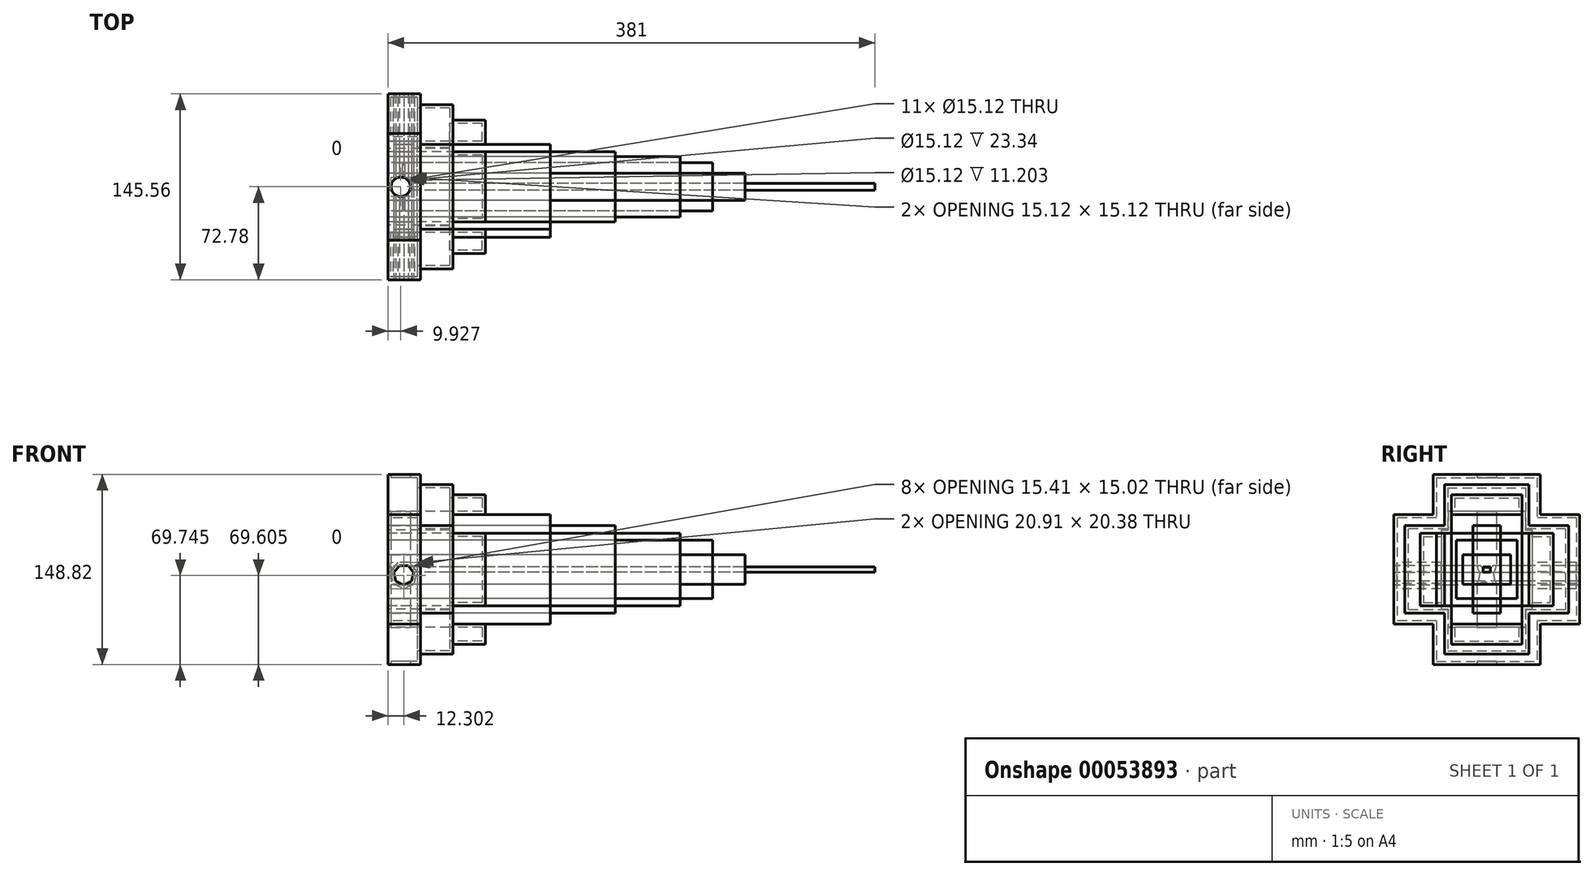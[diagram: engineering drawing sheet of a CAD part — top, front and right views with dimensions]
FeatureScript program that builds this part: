
annotation { "Feature Type Name" : "Feature", "Feature Type Description" : "" }
export const myFeature = defineFeature(function(context is Context, id is Id, definition is map)
    precondition{}
    {
        {
            var Q0;
            Q0=qCreatedBy(makeId("Top.planeOp"),FACE);
            var sketch = newSketch(context, id + "F0", { "sketchPlane" : qUnion([Q0])});
            skCircle(sketch, "E0", {"center": v(-6.98, 31.64) * mm, "radius": 25.79 * mm});
            skPoint(sketch, "E0.first.point", {"position": v(-32.77, 31.84) * mm});
            skPoint(sketch, "E0.second.point", {"position": v(18.77, 33.14) * mm});
            skPoint(sketch, "E0.third.point", {"position": v(-22.31, 52.38) * mm});
            skCircle(sketch, "E1", {"center": v(6.7, 18.5) * mm, "radius": 18.97 * mm});
            skPoint(sketch, "E1.second.point", {"position": v(2.52, 0) * mm});
            skCircle(sketch, "E2", {"center": v(-19.83, 38.18) * mm, "radius": 14.41 * mm});
            skCircle(sketch, "E3", {"center": v(-6.25, 28.75) * mm, "radius": 16.52 * mm});
            skPoint(sketch, "E3.third.point", {"position": v(-16.71, 41.55) * mm});
            skCircle(sketch, "E4", {"center": v(-7.59, 13.75) * mm, "radius": 15.06 * mm});
            skPoint(sketch, "E4.third.point", {"position": v(-8.92, 28.75) * mm});
            skCircle(sketch, "E5", {"center": v(-26.31, 19.65) * mm, "radius": 19.63 * mm});
            skCircle(sketch, "E6", {"center": v(3, 45.23) * mm, "radius": 20.34 * mm});
            skPoint(sketch, "E6.second.point", {"position": v(14.1, 62.27) * mm});
            skPoint(sketch, "E6.third.point", {"position": v(21.94, 37.81) * mm});
            skCircle(sketch, "E7", {"center": v(-21.54, 45.6) * mm, "radius": 21.06 * mm});
            skPoint(sketch, "E7.second.point", {"position": v(-35.94, 60.96) * mm});
            skPoint(sketch, "E7.third.point", {"position": v(-42.1, 50.13) * mm});
            skCircle(sketch, "E8", {"center": v(3.75, 38.24) * mm, "radius": 15.83 * mm});
            skPoint(sketch, "E8.second.point", {"position": v(18.2, 44.72) * mm});
            skPoint(sketch, "E8.third.point", {"position": v(6.7, 22.69) * mm});
            skCircle(sketch, "E9", {"center": v(-6.92, 15.23) * mm, "radius": 13.67 * mm});
            skPoint(sketch, "E9.first.point", {"position": v(-10.18, 1.96) * mm});
            skPoint(sketch, "E9.third.point", {"position": v(4.54, 22.69) * mm});
            skCircle(sketch, "E10", {"center": v(21.82, 32.35) * mm, "radius": 30.95 * mm});
            skPoint(sketch, "E10.second.point", {"position": v(52.56, 28.75) * mm});
            skPoint(sketch, "E10.third.point", {"position": v(26.6, 1.77) * mm});
            skCircle(sketch, "E11", {"center": v(-43.67, 28.86) * mm, "radius": 33.35 * mm});
            skPoint(sketch, "E11.first.point", {"position": v(-77.02, 28.66) * mm});
            skPoint(sketch, "E11.second.point", {"position": v(-10.4, 31.14) * mm});
            skPoint(sketch, "E11.third.point", {"position": v(-75.16, 39.86) * mm});
            skCircle(sketch, "E12", {"center": v(-4.85, 1.88) * mm, "radius": 27.18 * mm});
            skPoint(sketch, "E12.second.point", {"position": v(-5.13, -25.3) * mm});
            skPoint(sketch, "E12.third.point", {"position": v(-4.57, -25.3) * mm});
            skCircle(sketch, "E13", {"center": v(-7.9, 52.7) * mm, "radius": 23.97 * mm});
            skPoint(sketch, "E13.second.point", {"position": v(-8.92, 76.65) * mm});
            skPoint(sketch, "E13.third.point", {"position": v(-28.09, 65.62) * mm});
            skSolve(sketch);
        }
        {
            var Q0;
            Q0=qCreatedBy(makeId("Right.planeOp"),FACE);
            var sketch = newSketch(context, id + "F1", { "sketchPlane" : qUnion([Q0])});
            skLineSegment(sketch, "E14.rect.bottom", {"start": v(-23.76, 22.87) * mm, "end": v(23.76, 22.87) * mm});
            skLineSegment(sketch, "E14.rect.top", {"start": v(-23.76, -22.87) * mm, "end": v(23.76, -22.87) * mm});
            skLineSegment(sketch, "E14.rect.left", {"start": v(-23.76, 22.87) * mm, "end": v(-23.76, -22.87) * mm});
            skLineSegment(sketch, "E14.rect.right", {"start": v(23.76, 22.87) * mm, "end": v(23.76, -22.87) * mm});
            skPoint(sketch, "E14.rect.middle", {"position": v(0, 0) * mm});
            skLineSegment(sketch, "E15.rect.bottom", {"start": v(-10.69, 45.28) * mm, "end": v(10.69, 45.28) * mm});
            skLineSegment(sketch, "E15.rect.top", {"start": v(-10.69, -45.28) * mm, "end": v(10.69, -45.28) * mm});
            skLineSegment(sketch, "E15.rect.left", {"start": v(-10.69, 45.28) * mm, "end": v(-10.69, -45.28) * mm});
            skLineSegment(sketch, "E15.rect.right", {"start": v(10.69, 45.28) * mm, "end": v(10.69, -45.28) * mm});
            skLineSegment(sketch, "E16.rect.bottom", {"start": v(64.19, 34.26) * mm, "end": v(-64.19, 34.26) * mm});
            skLineSegment(sketch, "E16.rect.top", {"start": v(64.19, -34.26) * mm, "end": v(-64.19, -34.26) * mm});
            skLineSegment(sketch, "E16.rect.left", {"start": v(64.19, 34.26) * mm, "end": v(64.19, -34.26) * mm});
            skLineSegment(sketch, "E16.rect.right", {"start": v(-64.19, 34.26) * mm, "end": v(-64.19, -34.26) * mm});
            skLineSegment(sketch, "E17.rect.bottom", {"start": v(-33.1, 66.38) * mm, "end": v(33.1, 66.38) * mm});
            skLineSegment(sketch, "E17.rect.top", {"start": v(-33.1, -66.38) * mm, "end": v(33.1, -66.38) * mm});
            skLineSegment(sketch, "E17.rect.left", {"start": v(-33.1, 66.38) * mm, "end": v(-33.1, -66.38) * mm});
            skLineSegment(sketch, "E17.rect.right", {"start": v(33.1, 66.38) * mm, "end": v(33.1, -66.38) * mm});
            skLineSegment(sketch, "E18.rect.bottom", {"start": v(5.37, 6.07) * mm, "end": v(-5.37, 6.07) * mm});
            skLineSegment(sketch, "E18.rect.top", {"start": v(5.37, -6.07) * mm, "end": v(-5.37, -6.07) * mm});
            skLineSegment(sketch, "E18.rect.left", {"start": v(5.37, 6.07) * mm, "end": v(5.37, -6.07) * mm});
            skLineSegment(sketch, "E18.rect.right", {"start": v(-5.37, 6.07) * mm, "end": v(-5.37, -6.07) * mm});
            skLineSegment(sketch, "E19.rect.bottom", {"start": v(2.76, 2.15) * mm, "end": v(-2.76, 2.15) * mm});
            skLineSegment(sketch, "E19.rect.top", {"start": v(2.76, -2.15) * mm, "end": v(-2.76, -2.15) * mm});
            skLineSegment(sketch, "E19.rect.left", {"start": v(2.76, 2.15) * mm, "end": v(2.76, -2.15) * mm});
            skLineSegment(sketch, "E19.rect.right", {"start": v(-2.76, 2.15) * mm, "end": v(-2.76, -2.15) * mm});
            skLineSegment(sketch, "E20.rect.bottom", {"start": v(18.81, 11.67) * mm, "end": v(-18.81, 11.67) * mm});
            skLineSegment(sketch, "E20.rect.top", {"start": v(18.81, -11.67) * mm, "end": v(-18.81, -11.67) * mm});
            skLineSegment(sketch, "E20.rect.left", {"start": v(18.81, 11.67) * mm, "end": v(18.81, -11.67) * mm});
            skLineSegment(sketch, "E20.rect.right", {"start": v(-18.81, 11.67) * mm, "end": v(-18.81, -11.67) * mm});
            skLineSegment(sketch, "E21.rect.bottom", {"start": v(-52.14, 28.47) * mm, "end": v(52.14, 28.47) * mm});
            skLineSegment(sketch, "E21.rect.top", {"start": v(-52.14, -28.47) * mm, "end": v(52.14, -28.47) * mm});
            skLineSegment(sketch, "E21.rect.left", {"start": v(-52.14, 28.47) * mm, "end": v(-52.14, -28.47) * mm});
            skLineSegment(sketch, "E21.rect.right", {"start": v(52.14, 28.47) * mm, "end": v(52.14, -28.47) * mm});
            skLineSegment(sketch, "E22.rect.bottom", {"start": v(-27.5, 58.54) * mm, "end": v(27.5, 58.54) * mm});
            skLineSegment(sketch, "E22.rect.top", {"start": v(-27.5, -58.54) * mm, "end": v(27.5, -58.54) * mm});
            skLineSegment(sketch, "E22.rect.left", {"start": v(-27.5, 58.54) * mm, "end": v(-27.5, -58.54) * mm});
            skLineSegment(sketch, "E22.rect.right", {"start": v(27.5, 58.54) * mm, "end": v(27.5, -58.54) * mm});
            skLineSegment(sketch, "E23.rect.bottom", {"start": v(72.78, 42.85) * mm, "end": v(-72.78, 42.85) * mm});
            skLineSegment(sketch, "E23.rect.top", {"start": v(72.78, -42.85) * mm, "end": v(-72.78, -42.85) * mm});
            skLineSegment(sketch, "E23.rect.left", {"start": v(72.78, 42.85) * mm, "end": v(72.78, -42.85) * mm});
            skLineSegment(sketch, "E23.rect.right", {"start": v(-72.78, 42.85) * mm, "end": v(-72.78, -42.85) * mm});
            skLineSegment(sketch, "E24.rect.bottom", {"start": v(-41.87, 74.4) * mm, "end": v(41.87, 74.4) * mm});
            skLineSegment(sketch, "E24.rect.top", {"start": v(-41.87, -74.4) * mm, "end": v(41.87, -74.4) * mm});
            skLineSegment(sketch, "E24.rect.left", {"start": v(-41.87, 74.4) * mm, "end": v(-41.87, -74.4) * mm});
            skLineSegment(sketch, "E24.rect.right", {"start": v(41.87, 74.4) * mm, "end": v(41.87, -74.4) * mm});
            skSolve(sketch);
        }
        {
            var Q0;
            Q0 = qSketchRegion(id + "F1", true);
            extrude(context, id + "F2", {"entities" : qUnion([Q0]), "depth" : 25.4 * mm});
        }
        {
            var Q0;
            {var subQ0=sQuery(id+"F1.wireOp",EDGE,"E16.rect.right");Q0=makeQuery(id+"F1.imprint","IMPRINT",FACE,{"disambiguationData":[TD([[makeQuery(id+"F1.imprint","IMPRINT",EDGE,{"derivedFrom":subQ0}),1.0]])]});}
            var Q1;
            {var subQ8=sQuery(id+"F1.wireOp",EDGE,"E16.rect.left");Q1=makeQuery(id+"F1.imprint","IMPRINT",FACE,{"disambiguationData":[TD([[makeQuery(id+"F1.imprint","IMPRINT",EDGE,{"derivedFrom":subQ8}),-1.0]])]});}
            var Q2;
            {var subQ2=sQuery(id+"F1.wireOp",EDGE,"E17.rect.bottom");Q2=makeQuery(id+"F1.imprint","IMPRINT",FACE,{"disambiguationData":[TD([[makeQuery(id+"F1.imprint","IMPRINT",EDGE,{"derivedFrom":subQ2}),-1.0]])]});}
            var Q3;
            {var subQ2=sQuery(id+"F1.wireOp",EDGE,"E17.rect.top");Q3=makeQuery(id+"F1.imprint","IMPRINT",FACE,{"disambiguationData":[TD([[makeQuery(id+"F1.imprint","IMPRINT",EDGE,{"derivedFrom":subQ2}),1.0]])]});}
            extrude(context, id + "F3", {"entities" : qUnion([Q0, Q1, Q2, Q3]), "operationType" : NewBodyOperationType.ADD, "depth" : 50.8 * mm});
        }
        {
            var Q0;
            {var subQ0=sQuery(id+"F1.wireOp",EDGE,"E17.rect.right");var subQ1=sQuery(id+"F1.wireOp",EDGE,"E16.rect.bottom");var subQ2=makeQuery(id+"F1.imprint","INTERSECT",VERTEX,{"derivedFrom":[subQ1,subQ0]});Q0=makeQuery(id+"F1.imprint","IMPRINT",FACE,{"disambiguationData":[TD([[makeQuery(id+"F1.imprint","IMPRINT",EDGE,{"disambiguationData":[TD([[subQ2,-1.0]])],"derivedFrom":subQ1}),-1.0]])]});}
            var Q1;
            {var subQ0=sQuery(id+"F1.wireOp",EDGE,"E24.rect.right");var subQ1=sQuery(id+"F1.wireOp",EDGE,"E16.rect.bottom");var subQ2=makeQuery(id+"F1.imprint","INTERSECT",VERTEX,{"derivedFrom":[subQ1,subQ0]});Q1=makeQuery(id+"F1.imprint","IMPRINT",FACE,{"disambiguationData":[TD([[makeQuery(id+"F1.imprint","IMPRINT",EDGE,{"disambiguationData":[TD([[subQ2,-1.0]])],"derivedFrom":subQ1}),1.0]])]});}
            var Q2;
            {var subQ0=sQuery(id+"F1.wireOp",EDGE,"E17.rect.right");var subQ1=sQuery(id+"F1.wireOp",EDGE,"E16.rect.bottom");var subQ2=makeQuery(id+"F1.imprint","INTERSECT",VERTEX,{"derivedFrom":[subQ1,subQ0]});Q2=makeQuery(id+"F1.imprint","IMPRINT",FACE,{"disambiguationData":[TD([[makeQuery(id+"F1.imprint","IMPRINT",EDGE,{"disambiguationData":[TD([[subQ2,-1.0]])],"derivedFrom":subQ1}),1.0]])]});}
            var Q3;
            {var subQ0=sQuery(id+"F1.wireOp",EDGE,"E22.rect.left");var subQ1=sQuery(id+"F1.wireOp",EDGE,"E16.rect.bottom");var subQ2=makeQuery(id+"F1.imprint","INTERSECT",VERTEX,{"derivedFrom":[subQ1,subQ0]});Q3=makeQuery(id+"F1.imprint","IMPRINT",FACE,{"disambiguationData":[TD([[makeQuery(id+"F1.imprint","IMPRINT",EDGE,{"disambiguationData":[TD([[subQ2,-1.0]])],"derivedFrom":subQ1}),-1.0]])]});}
            var Q4;
            {var subQ0=sQuery(id+"F1.wireOp",EDGE,"E22.rect.left");var subQ1=sQuery(id+"F1.wireOp",EDGE,"E16.rect.bottom");var subQ2=makeQuery(id+"F1.imprint","INTERSECT",VERTEX,{"derivedFrom":[subQ1,subQ0]});Q4=makeQuery(id+"F1.imprint","IMPRINT",FACE,{"disambiguationData":[TD([[makeQuery(id+"F1.imprint","IMPRINT",EDGE,{"disambiguationData":[TD([[subQ2,-1.0]])],"derivedFrom":subQ1}),1.0]])]});}
            var Q5;
            {var subQ0=sQuery(id+"F1.wireOp",EDGE,"E17.rect.left");var subQ1=sQuery(id+"F1.wireOp",EDGE,"E16.rect.bottom");var subQ2=makeQuery(id+"F1.imprint","INTERSECT",VERTEX,{"derivedFrom":[subQ1,subQ0]});Q5=makeQuery(id+"F1.imprint","IMPRINT",FACE,{"disambiguationData":[TD([[makeQuery(id+"F1.imprint","IMPRINT",EDGE,{"disambiguationData":[TD([[subQ2,-1.0]])],"derivedFrom":subQ1}),1.0]])]});}
            var Q6;
            {var subQ0=sQuery(id+"F1.wireOp",EDGE,"E17.rect.left");var subQ1=sQuery(id+"F1.wireOp",EDGE,"E16.rect.top");var subQ2=makeQuery(id+"F1.imprint","INTERSECT",VERTEX,{"derivedFrom":[subQ1,subQ0]});Q6=makeQuery(id+"F1.imprint","IMPRINT",FACE,{"disambiguationData":[TD([[makeQuery(id+"F1.imprint","IMPRINT",EDGE,{"disambiguationData":[TD([[subQ2,-1.0]])],"derivedFrom":subQ1}),-1.0]])]});}
            var Q7;
            {var subQ0=sQuery(id+"F1.wireOp",EDGE,"E22.rect.left");var subQ1=sQuery(id+"F1.wireOp",EDGE,"E16.rect.top");var subQ2=makeQuery(id+"F1.imprint","INTERSECT",VERTEX,{"derivedFrom":[subQ1,subQ0]});Q7=makeQuery(id+"F1.imprint","IMPRINT",FACE,{"disambiguationData":[TD([[makeQuery(id+"F1.imprint","IMPRINT",EDGE,{"disambiguationData":[TD([[subQ2,-1.0]])],"derivedFrom":subQ1}),-1.0]])]});}
            var Q8;
            {var subQ0=sQuery(id+"F1.wireOp",EDGE,"E22.rect.left");var subQ1=sQuery(id+"F1.wireOp",EDGE,"E16.rect.top");var subQ2=makeQuery(id+"F1.imprint","INTERSECT",VERTEX,{"derivedFrom":[subQ1,subQ0]});Q8=makeQuery(id+"F1.imprint","IMPRINT",FACE,{"disambiguationData":[TD([[makeQuery(id+"F1.imprint","IMPRINT",EDGE,{"disambiguationData":[TD([[subQ2,-1.0]])],"derivedFrom":subQ1}),1.0]])]});}
            var Q9;
            {var subQ0=sQuery(id+"F1.wireOp",EDGE,"E17.rect.right");var subQ1=sQuery(id+"F1.wireOp",EDGE,"E16.rect.top");var subQ2=makeQuery(id+"F1.imprint","INTERSECT",VERTEX,{"derivedFrom":[subQ1,subQ0]});Q9=makeQuery(id+"F1.imprint","IMPRINT",FACE,{"disambiguationData":[TD([[makeQuery(id+"F1.imprint","IMPRINT",EDGE,{"disambiguationData":[TD([[subQ2,-1.0]])],"derivedFrom":subQ1}),1.0]])]});}
            var Q10;
            {var subQ0=sQuery(id+"F1.wireOp",EDGE,"E17.rect.right");var subQ1=sQuery(id+"F1.wireOp",EDGE,"E16.rect.top");var subQ2=makeQuery(id+"F1.imprint","INTERSECT",VERTEX,{"derivedFrom":[subQ1,subQ0]});Q10=makeQuery(id+"F1.imprint","IMPRINT",FACE,{"disambiguationData":[TD([[makeQuery(id+"F1.imprint","IMPRINT",EDGE,{"disambiguationData":[TD([[subQ2,-1.0]])],"derivedFrom":subQ1}),-1.0]])]});}
            var Q11;
            {var subQ0=sQuery(id+"F1.wireOp",EDGE,"E24.rect.right");var subQ1=sQuery(id+"F1.wireOp",EDGE,"E16.rect.top");var subQ2=makeQuery(id+"F1.imprint","INTERSECT",VERTEX,{"derivedFrom":[subQ1,subQ0]});Q11=makeQuery(id+"F1.imprint","IMPRINT",FACE,{"disambiguationData":[TD([[makeQuery(id+"F1.imprint","IMPRINT",EDGE,{"disambiguationData":[TD([[subQ2,-1.0]])],"derivedFrom":subQ1}),-1.0]])]});}
            extrude(context, id + "F4", {"entities" : qUnion([Q0, Q1, Q2, Q3, Q4, Q5, Q6, Q7, Q8, Q9, Q10, Q11]), "operationType" : NewBodyOperationType.ADD, "depth" : 50.8 * mm});
        }
        {
            var Q0;
            {var subQ0=sQuery(id+"F1.wireOp",EDGE,"E21.rect.right");Q0=makeQuery(id+"F1.imprint","IMPRINT",FACE,{"disambiguationData":[TD([[makeQuery(id+"F1.imprint","IMPRINT",EDGE,{"derivedFrom":subQ0}),-1.0]])]});}
            var Q1;
            {var subQ0=sQuery(id+"F1.wireOp",EDGE,"E21.rect.bottom");var subQ1=sQuery(id+"F1.wireOp",EDGE,"E17.rect.right");var subQ2=makeQuery(id+"F1.imprint","INTERSECT",VERTEX,{"derivedFrom":[subQ1,subQ0]});Q1=makeQuery(id+"F1.imprint","IMPRINT",FACE,{"disambiguationData":[TD([[makeQuery(id+"F1.imprint","IMPRINT",EDGE,{"disambiguationData":[TD([[subQ2,-1.0]])],"derivedFrom":subQ1}),1.0]])]});}
            var Q2;
            {var subQ6=sQuery(id+"F1.wireOp",EDGE,"E15.rect.bottom");Q2=makeQuery(id+"F1.imprint","IMPRINT",FACE,{"disambiguationData":[TD([[makeQuery(id+"F1.imprint","IMPRINT",EDGE,{"derivedFrom":subQ6}),1.0]])]});}
            var Q3;
            {var subQ0=sQuery(id+"F1.wireOp",EDGE,"E21.rect.left");Q3=makeQuery(id+"F1.imprint","IMPRINT",FACE,{"disambiguationData":[TD([[makeQuery(id+"F1.imprint","IMPRINT",EDGE,{"derivedFrom":subQ0}),1.0]])]});}
            var Q4;
            {var subQ0=sQuery(id+"F1.wireOp",EDGE,"E21.rect.bottom");var subQ1=sQuery(id+"F1.wireOp",EDGE,"E17.rect.left");var subQ2=makeQuery(id+"F1.imprint","INTERSECT",VERTEX,{"derivedFrom":[subQ1,subQ0]});Q4=makeQuery(id+"F1.imprint","IMPRINT",FACE,{"disambiguationData":[TD([[makeQuery(id+"F1.imprint","IMPRINT",EDGE,{"disambiguationData":[TD([[subQ2,-1.0]])],"derivedFrom":subQ1}),-1.0]])]});}
            var Q5;
            {var subQ2=sQuery(id+"F1.wireOp",EDGE,"E15.rect.top");Q5=makeQuery(id+"F1.imprint","IMPRINT",FACE,{"disambiguationData":[TD([[makeQuery(id+"F1.imprint","IMPRINT",EDGE,{"derivedFrom":subQ2}),-1.0]])]});}
            var Q6;
            {var subQ0=sQuery(id+"F1.wireOp",EDGE,"E15.rect.top");Q6=makeQuery(id+"F1.imprint","IMPRINT",FACE,{"disambiguationData":[TD([[makeQuery(id+"F1.imprint","IMPRINT",EDGE,{"derivedFrom":subQ0}),1.0]])]});}
            var Q7;
            {var subQ0=sQuery(id+"F1.wireOp",EDGE,"E15.rect.bottom");Q7=makeQuery(id+"F1.imprint","IMPRINT",FACE,{"disambiguationData":[TD([[makeQuery(id+"F1.imprint","IMPRINT",EDGE,{"derivedFrom":subQ0}),-1.0]])]});}
            extrude(context, id + "F5", {"entities" : qUnion([Q0, Q1, Q2, Q3, Q4, Q5, Q6, Q7]), "operationType" : NewBodyOperationType.ADD, "depth" : 76.2 * mm});
        }
        {
            var Q0;
            {var subQ0=sQuery(id+"F1.wireOp",EDGE,"E23.rect.bottom");var subQ1=sQuery(id+"F1.wireOp",EDGE,"E15.rect.right");var subQ2=makeQuery(id+"F1.imprint","INTERSECT",VERTEX,{"derivedFrom":[subQ1,subQ0]});Q0=makeQuery(id+"F1.imprint","IMPRINT",FACE,{"disambiguationData":[TD([[makeQuery(id+"F1.imprint","IMPRINT",EDGE,{"disambiguationData":[TD([[subQ2,-1.0]])],"derivedFrom":subQ1}),1.0]])]});}
            var Q1;
            {var subQ0=sQuery(id+"F1.wireOp",EDGE,"E23.rect.bottom");var subQ1=sQuery(id+"F1.wireOp",EDGE,"E15.rect.left");var subQ2=makeQuery(id+"F1.imprint","INTERSECT",VERTEX,{"derivedFrom":[subQ1,subQ0]});Q1=makeQuery(id+"F1.imprint","IMPRINT",FACE,{"disambiguationData":[TD([[makeQuery(id+"F1.imprint","IMPRINT",EDGE,{"disambiguationData":[TD([[subQ2,-1.0]])],"derivedFrom":subQ1}),1.0]])]});}
            var Q2;
            {var subQ0=sQuery(id+"F1.wireOp",EDGE,"E23.rect.bottom");var subQ1=sQuery(id+"F1.wireOp",EDGE,"E15.rect.left");var subQ2=makeQuery(id+"F1.imprint","INTERSECT",VERTEX,{"derivedFrom":[subQ1,subQ0]});Q2=makeQuery(id+"F1.imprint","IMPRINT",FACE,{"disambiguationData":[TD([[makeQuery(id+"F1.imprint","IMPRINT",EDGE,{"disambiguationData":[TD([[subQ2,-1.0]])],"derivedFrom":subQ1}),-1.0]])]});}
            var Q3;
            {var subQ0=sQuery(id+"F1.wireOp",EDGE,"E16.rect.bottom");var subQ1=sQuery(id+"F1.wireOp",EDGE,"E15.rect.right");var subQ2=makeQuery(id+"F1.imprint","INTERSECT",VERTEX,{"derivedFrom":[subQ1,subQ0]});Q3=makeQuery(id+"F1.imprint","IMPRINT",FACE,{"disambiguationData":[TD([[makeQuery(id+"F1.imprint","IMPRINT",EDGE,{"disambiguationData":[TD([[subQ2,-1.0]])],"derivedFrom":subQ1}),1.0]])]});}
            var Q4;
            {var subQ0=sQuery(id+"F1.wireOp",EDGE,"E16.rect.bottom");var subQ1=sQuery(id+"F1.wireOp",EDGE,"E15.rect.left");var subQ2=makeQuery(id+"F1.imprint","INTERSECT",VERTEX,{"derivedFrom":[subQ1,subQ0]});Q4=makeQuery(id+"F1.imprint","IMPRINT",FACE,{"disambiguationData":[TD([[makeQuery(id+"F1.imprint","IMPRINT",EDGE,{"disambiguationData":[TD([[subQ2,-1.0]])],"derivedFrom":subQ1}),-1.0]])]});}
            var Q5;
            {var subQ0=sQuery(id+"F1.wireOp",EDGE,"E21.rect.bottom");var subQ1=sQuery(id+"F1.wireOp",EDGE,"E17.rect.left");var subQ2=makeQuery(id+"F1.imprint","INTERSECT",VERTEX,{"derivedFrom":[subQ1,subQ0]});Q5=makeQuery(id+"F1.imprint","IMPRINT",FACE,{"disambiguationData":[TD([[makeQuery(id+"F1.imprint","IMPRINT",EDGE,{"disambiguationData":[TD([[subQ2,-1.0]])],"derivedFrom":subQ1}),1.0]])]});}
            var Q6;
            {var subQ0=sQuery(id+"F1.wireOp",EDGE,"E21.rect.bottom");var subQ1=sQuery(id+"F1.wireOp",EDGE,"E17.rect.right");var subQ2=makeQuery(id+"F1.imprint","INTERSECT",VERTEX,{"derivedFrom":[subQ1,subQ0]});Q6=makeQuery(id+"F1.imprint","IMPRINT",FACE,{"disambiguationData":[TD([[makeQuery(id+"F1.imprint","IMPRINT",EDGE,{"disambiguationData":[TD([[subQ2,-1.0]])],"derivedFrom":subQ1}),-1.0]])]});}
            var Q7;
            {var subQ0=sQuery(id+"F1.wireOp",EDGE,"E21.rect.top");var subQ1=sQuery(id+"F1.wireOp",EDGE,"E15.rect.right");var subQ2=makeQuery(id+"F1.imprint","INTERSECT",VERTEX,{"derivedFrom":[subQ1,subQ0]});Q7=makeQuery(id+"F1.imprint","IMPRINT",FACE,{"disambiguationData":[TD([[makeQuery(id+"F1.imprint","IMPRINT",EDGE,{"disambiguationData":[TD([[subQ2,-1.0]])],"derivedFrom":subQ1}),1.0]])]});}
            var Q8;
            {var subQ0=sQuery(id+"F1.wireOp",EDGE,"E16.rect.top");var subQ1=sQuery(id+"F1.wireOp",EDGE,"E15.rect.right");var subQ2=makeQuery(id+"F1.imprint","INTERSECT",VERTEX,{"derivedFrom":[subQ1,subQ0]});Q8=makeQuery(id+"F1.imprint","IMPRINT",FACE,{"disambiguationData":[TD([[makeQuery(id+"F1.imprint","IMPRINT",EDGE,{"disambiguationData":[TD([[subQ2,-1.0]])],"derivedFrom":subQ1}),1.0]])]});}
            var Q9;
            {var subQ0=sQuery(id+"F1.wireOp",EDGE,"E16.rect.top");var subQ1=sQuery(id+"F1.wireOp",EDGE,"E15.rect.left");var subQ2=makeQuery(id+"F1.imprint","INTERSECT",VERTEX,{"derivedFrom":[subQ1,subQ0]});Q9=makeQuery(id+"F1.imprint","IMPRINT",FACE,{"disambiguationData":[TD([[makeQuery(id+"F1.imprint","IMPRINT",EDGE,{"disambiguationData":[TD([[subQ2,-1.0]])],"derivedFrom":subQ1}),1.0]])]});}
            var Q10;
            {var subQ0=sQuery(id+"F1.wireOp",EDGE,"E16.rect.top");var subQ1=sQuery(id+"F1.wireOp",EDGE,"E15.rect.left");var subQ2=makeQuery(id+"F1.imprint","INTERSECT",VERTEX,{"derivedFrom":[subQ1,subQ0]});Q10=makeQuery(id+"F1.imprint","IMPRINT",FACE,{"disambiguationData":[TD([[makeQuery(id+"F1.imprint","IMPRINT",EDGE,{"disambiguationData":[TD([[subQ2,-1.0]])],"derivedFrom":subQ1}),-1.0]])]});}
            var Q11;
            {var subQ0=sQuery(id+"F1.wireOp",EDGE,"E21.rect.top");var subQ1=sQuery(id+"F1.wireOp",EDGE,"E15.rect.left");var subQ2=makeQuery(id+"F1.imprint","INTERSECT",VERTEX,{"derivedFrom":[subQ1,subQ0]});Q11=makeQuery(id+"F1.imprint","IMPRINT",FACE,{"disambiguationData":[TD([[makeQuery(id+"F1.imprint","IMPRINT",EDGE,{"disambiguationData":[TD([[subQ2,-1.0]])],"derivedFrom":subQ1}),-1.0]])]});}
            extrude(context, id + "F6", {"entities" : qUnion([Q0, Q1, Q2, Q3, Q4, Q5, Q6, Q7, Q8, Q9, Q10, Q11]), "depth" : 127 * mm});
        }
        {
            var Q0;
            {var subQ0=sQuery(id+"F1.wireOp",EDGE,"E16.rect.bottom");var subQ1=sQuery(id+"F1.wireOp",EDGE,"E15.rect.left");var subQ2=makeQuery(id+"F1.imprint","INTERSECT",VERTEX,{"derivedFrom":[subQ1,subQ0]});Q0=makeQuery(id+"F1.imprint","IMPRINT",FACE,{"disambiguationData":[TD([[makeQuery(id+"F1.imprint","IMPRINT",EDGE,{"disambiguationData":[TD([[subQ2,-1.0]])],"derivedFrom":subQ1}),1.0]])]});}
            var Q1;
            {var subQ5=sQuery(id+"F1.wireOp",EDGE,"E14.rect.left");Q1=makeQuery(id+"F1.imprint","IMPRINT",FACE,{"disambiguationData":[TD([[makeQuery(id+"F1.imprint","IMPRINT",EDGE,{"derivedFrom":subQ5}),-1.0]])]});}
            var Q2;
            {var subQ0=sQuery(id+"F1.wireOp",EDGE,"E21.rect.top");var subQ1=sQuery(id+"F1.wireOp",EDGE,"E15.rect.left");var subQ2=makeQuery(id+"F1.imprint","INTERSECT",VERTEX,{"derivedFrom":[subQ1,subQ0]});Q2=makeQuery(id+"F1.imprint","IMPRINT",FACE,{"disambiguationData":[TD([[makeQuery(id+"F1.imprint","IMPRINT",EDGE,{"disambiguationData":[TD([[subQ2,-1.0]])],"derivedFrom":subQ1}),1.0]])]});}
            var Q3;
            {var subQ5=sQuery(id+"F1.wireOp",EDGE,"E14.rect.right");Q3=makeQuery(id+"F1.imprint","IMPRINT",FACE,{"disambiguationData":[TD([[makeQuery(id+"F1.imprint","IMPRINT",EDGE,{"derivedFrom":subQ5}),1.0]])]});}
            extrude(context, id + "F7", {"entities" : qUnion([Q0, Q1, Q2, Q3]), "depth" : 177.8 * mm});
        }
        {
            var Q0;
            {var subQ0=sQuery(id+"F1.wireOp",EDGE,"E15.rect.left");var subQ1=sQuery(id+"F1.wireOp",EDGE,"E14.rect.bottom");var subQ2=makeQuery(id+"F1.imprint","INTERSECT",VERTEX,{"derivedFrom":[subQ1,subQ0]});Q0=makeQuery(id+"F1.imprint","IMPRINT",FACE,{"disambiguationData":[TD([[makeQuery(id+"F1.imprint","IMPRINT",EDGE,{"disambiguationData":[TD([[subQ2,-1.0]])],"derivedFrom":subQ1}),1.0]])]});}
            var Q1;
            {var subQ5=sQuery(id+"F1.wireOp",EDGE,"E14.rect.right");Q1=makeQuery(id+"F1.imprint","IMPRINT",FACE,{"disambiguationData":[TD([[makeQuery(id+"F1.imprint","IMPRINT",EDGE,{"derivedFrom":subQ5}),-1.0]])]});}
            var Q2;
            {var subQ0=sQuery(id+"F1.wireOp",EDGE,"E15.rect.left");var subQ1=sQuery(id+"F1.wireOp",EDGE,"E14.rect.top");var subQ2=makeQuery(id+"F1.imprint","INTERSECT",VERTEX,{"derivedFrom":[subQ1,subQ0]});Q2=makeQuery(id+"F1.imprint","IMPRINT",FACE,{"disambiguationData":[TD([[makeQuery(id+"F1.imprint","IMPRINT",EDGE,{"disambiguationData":[TD([[subQ2,-1.0]])],"derivedFrom":subQ1}),-1.0]])]});}
            var Q3;
            {var subQ6=sQuery(id+"F1.wireOp",EDGE,"E14.rect.left");Q3=makeQuery(id+"F1.imprint","IMPRINT",FACE,{"disambiguationData":[TD([[makeQuery(id+"F1.imprint","IMPRINT",EDGE,{"derivedFrom":subQ6}),1.0]])]});}
            extrude(context, id + "F8", {"entities" : qUnion([Q0, Q1, Q2, Q3]), "depth" : 228.6 * mm});
        }
        {
            var Q0;
            {var subQ0=sQuery(id+"F1.wireOp",EDGE,"E15.rect.left");var subQ1=sQuery(id+"F1.wireOp",EDGE,"E14.rect.bottom");var subQ2=makeQuery(id+"F1.imprint","INTERSECT",VERTEX,{"derivedFrom":[subQ1,subQ0]});Q0=makeQuery(id+"F1.imprint","IMPRINT",FACE,{"disambiguationData":[TD([[makeQuery(id+"F1.imprint","IMPRINT",EDGE,{"disambiguationData":[TD([[subQ2,-1.0]])],"derivedFrom":subQ1}),-1.0]])]});}
            var Q1;
            {var subQ5=sQuery(id+"F1.wireOp",EDGE,"E20.rect.left");Q1=makeQuery(id+"F1.imprint","IMPRINT",FACE,{"disambiguationData":[TD([[makeQuery(id+"F1.imprint","IMPRINT",EDGE,{"derivedFrom":subQ5}),-1.0]])]});}
            var Q2;
            {var subQ0=sQuery(id+"F1.wireOp",EDGE,"E15.rect.left");var subQ1=sQuery(id+"F1.wireOp",EDGE,"E14.rect.top");var subQ2=makeQuery(id+"F1.imprint","INTERSECT",VERTEX,{"derivedFrom":[subQ1,subQ0]});Q2=makeQuery(id+"F1.imprint","IMPRINT",FACE,{"disambiguationData":[TD([[makeQuery(id+"F1.imprint","IMPRINT",EDGE,{"disambiguationData":[TD([[subQ2,-1.0]])],"derivedFrom":subQ1}),1.0]])]});}
            var Q3;
            {var subQ5=sQuery(id+"F1.wireOp",EDGE,"E20.rect.right");Q3=makeQuery(id+"F1.imprint","IMPRINT",FACE,{"disambiguationData":[TD([[makeQuery(id+"F1.imprint","IMPRINT",EDGE,{"derivedFrom":subQ5}),1.0]])]});}
            extrude(context, id + "F9", {"entities" : qUnion([Q0, Q1, Q2, Q3]), "depth" : 254 * mm});
        }
        {
            var Q0;
            Q0=makeQuery(id+"F1.imprint","IMPRINT",FACE,{"disambiguationData":[TD([[makeQuery(id+"F1.imprint","IMPRINT",EDGE,{"derivedFrom":sQuery(id+"F1.wireOp",EDGE,"E18.rect.bottom")}),-1.0]])]});
            var Q1;
            Q1=makeQuery(id+"F1.imprint","IMPRINT",FACE,{"disambiguationData":[TD([[makeQuery(id+"F1.imprint","IMPRINT",EDGE,{"derivedFrom":sQuery(id+"F1.wireOp",EDGE,"E18.rect.bottom")}),1.0]])]});
            extrude(context, id + "F10", {"entities" : qUnion([Q0, Q1]), "depth" : 279.4 * mm});
        }
        {
            var Q0;
            Q0=makeQuery(id+"F1.imprint","IMPRINT",FACE,{"disambiguationData":[TD([[makeQuery(id+"F1.imprint","IMPRINT",EDGE,{"derivedFrom":sQuery(id+"F1.wireOp",EDGE,"E19.rect.bottom")}),1.0]])]});
            extrude(context, id + "F11", {"entities" : qUnion([Q0]), "depth" : 279.4 * mm});
        }
        {
            var Q0;
            Q0=makeQuery(id+"F1.imprint","IMPRINT",FACE,{"disambiguationData":[TD([[makeQuery(id+"F1.imprint","IMPRINT",EDGE,{"derivedFrom":sQuery(id+"F1.wireOp",EDGE,"E19.rect.bottom")}),1.0]])]});
            extrude(context, id + "F12", {"entities" : qUnion([Q0]), "depth" : 381 * mm});
        }
        {
            var Q0;
            Q0=makeQuery(id+"F6.opExtrude","SWEPT_FACE",FACE,{"disambiguationData":[OSD([sQuery(id+"F1.wireOp",EDGE,"E17.rect.left")])]});
            extrude(context, id + "F13", {"entities" : qUnion([Q0]), "depth" : 6.35 * mm});
        }
        {
            var Q0;
            Q0=makeQuery(id+"F2.opExtrude","SWEPT_FACE",FACE,{"disambiguationData":[OSD([sQuery(id+"F1.wireOp",EDGE,"E23.rect.right")])]});
            var sketch = newSketch(context, id + "F14", { "sketchPlane" : qUnion([Q0])});
            skCircle(sketch, "E25.cCircle", {"center": v(12.3, -4.27) * mm, "radius": 7.12 * mm, "construction": true});
            skLineSegment(sketch, "E25.0", {"start": v(8.87, 2.85) * mm, "end": v(15.73, 2.85) * mm});
            skLineSegment(sketch, "E25.1", {"start": v(15.73, 2.85) * mm, "end": v(20, -2.52) * mm});
            skLineSegment(sketch, "E25.2", {"start": v(20, -2.52) * mm, "end": v(18.48, -9.2) * mm});
            skLineSegment(sketch, "E25.3", {"start": v(18.48, -9.2) * mm, "end": v(12.3, -12.18) * mm});
            skLineSegment(sketch, "E25.4", {"start": v(12.3, -12.18) * mm, "end": v(6.12, -9.2) * mm});
            skLineSegment(sketch, "E25.5", {"start": v(6.12, -9.2) * mm, "end": v(4.6, -2.52) * mm});
            skLineSegment(sketch, "E25.6", {"start": v(4.6, -2.52) * mm, "end": v(8.87, 2.85) * mm});
            skPoint(sketch, "E25.0.midPoint", {"position": v(12.3, 2.85) * mm});
            skSolve(sketch);
        }
        {
            var Q0;
            Q0 = qSketchRegion(id + "F14", true);
            extrude(context, id + "F15", {"entities" : qUnion([Q0]), "operationType" : NewBodyOperationType.REMOVE, "endBound" : BoundingType.THROUGH_ALL, "oppositeDirection" : true, "depth" : 25.4 * mm});
        }
        {
            var Q0;
            {var subQ0=sQuery(id+"F1.wireOp",EDGE,"E23.rect.top");var subQ1=sQuery(id+"F1.wireOp",EDGE,"E22.rect.right");var subQ2=sQuery(id+"F1.wireOp",EDGE,"E22.rect.left");var subQ3=sQuery(id+"F1.wireOp",EDGE,"E22.rect.top");var subQ4=sQuery(id+"F1.wireOp",EDGE,"E23.rect.bottom");var subQ5=sQuery(id+"F1.wireOp",EDGE,"E22.rect.bottom");var subQ6=sQuery(id+"F1.wireOp",EDGE,"E21.rect.right");var subQ7=sQuery(id+"F1.wireOp",EDGE,"E21.rect.top");var subQ8=sQuery(id+"F1.wireOp",EDGE,"E21.rect.bottom");var subQ9=sQuery(id+"F1.wireOp",EDGE,"E17.rect.right");var subQ10=sQuery(id+"F1.wireOp",EDGE,"E21.rect.left");var subQ11=sQuery(id+"F1.wireOp",EDGE,"E17.rect.left");var subQ12=sQuery(id+"F1.wireOp",EDGE,"E24.rect.left");var subQ13=sQuery(id+"F1.wireOp",EDGE,"E16.rect.top");var subQ14=sQuery(id+"F1.wireOp",EDGE,"E24.rect.right");var subQ15=sQuery(id+"F1.wireOp",EDGE,"E16.rect.bottom");var subQ16=sQuery(id+"F1.wireOp",EDGE,"E17.rect.top");var subQ17=sQuery(id+"F1.wireOp",EDGE,"E17.rect.bottom");var subQ18=sQuery(id+"F1.wireOp",EDGE,"E16.rect.right");var subQ19=sQuery(id+"F1.wireOp",EDGE,"E16.rect.left");Q0=makeQuery(id+"F5.boolean.opBoolean","MERGE",FACE,{"derivedFrom":[makeQuery(id+"F4.boolean.opBoolean","MERGE",FACE,{"derivedFrom":[makeQuery(id+"F3.boolean.opBoolean","MERGE",FACE,{"derivedFrom":[makeQuery(id+"F2.opExtrude","CAP_FACE",FACE,{"disambiguationData":[OSD([subQ15,subQ13,subQ19,subQ18,subQ17,subQ16,subQ11,subQ9,subQ4,subQ0,sQuery(id+"F1.wireOp",EDGE,"E23.rect.left"),sQuery(id+"F1.wireOp",EDGE,"E23.rect.right"),sQuery(id+"F1.wireOp",EDGE,"E24.rect.bottom"),sQuery(id+"F1.wireOp",EDGE,"E24.rect.top"),subQ12,subQ14])],"isStart":true}),makeQuery(id+"F3.opExtrude","CAP_FACE",FACE,{"disambiguationData":[OSD([subQ15,subQ13,subQ19,subQ8,subQ7,subQ6,subQ14])],"isStart":true}),makeQuery(id+"F3.opExtrude","CAP_FACE",FACE,{"disambiguationData":[OSD([subQ15,subQ13,subQ18,subQ8,subQ7,subQ10,subQ12])],"isStart":true}),makeQuery(id+"F3.opExtrude","CAP_FACE",FACE,{"disambiguationData":[OSD([subQ17,subQ11,subQ9,subQ5,subQ2,subQ1,subQ4])],"isStart":true}),makeQuery(id+"F3.opExtrude","CAP_FACE",FACE,{"disambiguationData":[OSD([subQ16,subQ11,subQ9,subQ3,subQ2,subQ1,subQ0])],"isStart":true})]}),makeQuery(id+"F4.opExtrude","CAP_FACE",FACE,{"disambiguationData":[OSD([subQ15,subQ9,subQ8,subQ1,subQ4,subQ14])],"isStart":true}),makeQuery(id+"F4.opExtrude","CAP_FACE",FACE,{"disambiguationData":[OSD([subQ15,subQ11,subQ8,subQ2,subQ4,subQ12])],"isStart":true}),makeQuery(id+"F4.opExtrude","CAP_FACE",FACE,{"disambiguationData":[OSD([subQ13,subQ9,subQ7,subQ1,subQ0,subQ14])],"isStart":true}),makeQuery(id+"F4.opExtrude","CAP_FACE",FACE,{"disambiguationData":[OSD([subQ13,subQ11,subQ7,subQ2,subQ0,subQ12])],"isStart":true})]}),makeQuery(id+"F5.opExtrude","CAP_FACE",FACE,{"disambiguationData":[OSD([subQ11,subQ8,subQ7,subQ10])],"isStart":true}),makeQuery(id+"F5.opExtrude","CAP_FACE",FACE,{"disambiguationData":[OSD([subQ9,subQ8,subQ7,subQ6])],"isStart":true}),makeQuery(id+"F5.opExtrude","CAP_FACE",FACE,{"disambiguationData":[OSD([subQ5,subQ2,subQ1,subQ4])],"isStart":true}),makeQuery(id+"F5.opExtrude","CAP_FACE",FACE,{"disambiguationData":[OSD([subQ3,subQ2,subQ1,subQ0])],"isStart":true})]});}
            shell(context, id + "F16", {"entities" : qUnion([Q0]), "thickness" : 2.54 * mm});
        }
        {
            var Q0;
            Q0=makeQuery(id+"F2.opExtrude","SWEPT_FACE",FACE,{"disambiguationData":[OSD([sQuery(id+"F1.wireOp",EDGE,"E24.rect.top")])]});
            var sketch = newSketch(context, id + "F17", { "sketchPlane" : qUnion([Q0])});
            skCircle(sketch, "E26", {"center": v(9.93, 0) * mm, "radius": 7.56 * mm});
            skSolve(sketch);
        }
        {
            var Q0;
            Q0 = qSketchRegion(id + "F17", true);
            extrude(context, id + "F18", {"entities" : qUnion([Q0]), "operationType" : NewBodyOperationType.REMOVE, "oppositeDirection" : true, "depth" : 203.2 * mm});
        }
    });
